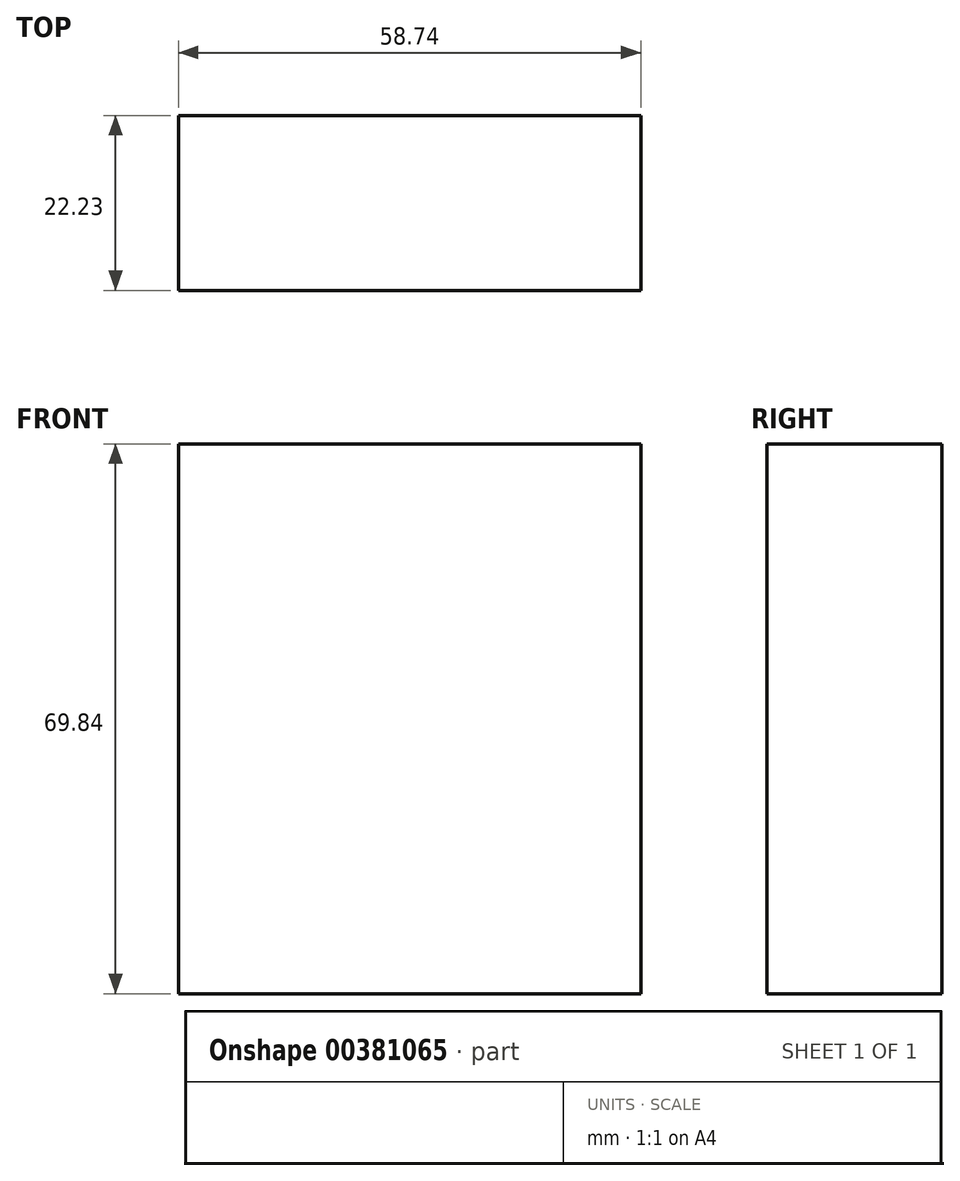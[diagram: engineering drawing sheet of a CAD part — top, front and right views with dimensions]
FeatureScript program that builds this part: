
annotation { "Feature Type Name" : "Feature", "Feature Type Description" : "" }
export const myFeature = defineFeature(function(context is Context, id is Id, definition is map)
    precondition{}
    {
        {
            var Q0;
            Q0=qCreatedBy(makeId("Front.planeOp"),FACE);
            var sketch = newSketch(context, id + "F0", { "sketchPlane" : qUnion([Q0])});
            skLineSegment(sketch, "E0.bottom", {"start": v(29.37, 34.92) * mm, "end": v(-29.37, 34.92) * mm});
            skLineSegment(sketch, "E0.top", {"start": v(29.37, -34.93) * mm, "end": v(-29.37, -34.93) * mm});
            skLineSegment(sketch, "E0.left", {"start": v(29.37, 34.92) * mm, "end": v(29.37, -34.93) * mm});
            skLineSegment(sketch, "E0.right", {"start": v(-29.37, 34.92) * mm, "end": v(-29.37, -34.93) * mm});
            skPoint(sketch, "E0.middle", {"position": v(0, 0) * mm});
            skSolve(sketch);
        }
        {
            var Q0;
            Q0 = qSketchRegion(id + "F0", true);
            extrude(context, id + "F1", {"entities" : qUnion([Q0]), "depth" : 22.22 * mm});
        }
    });
